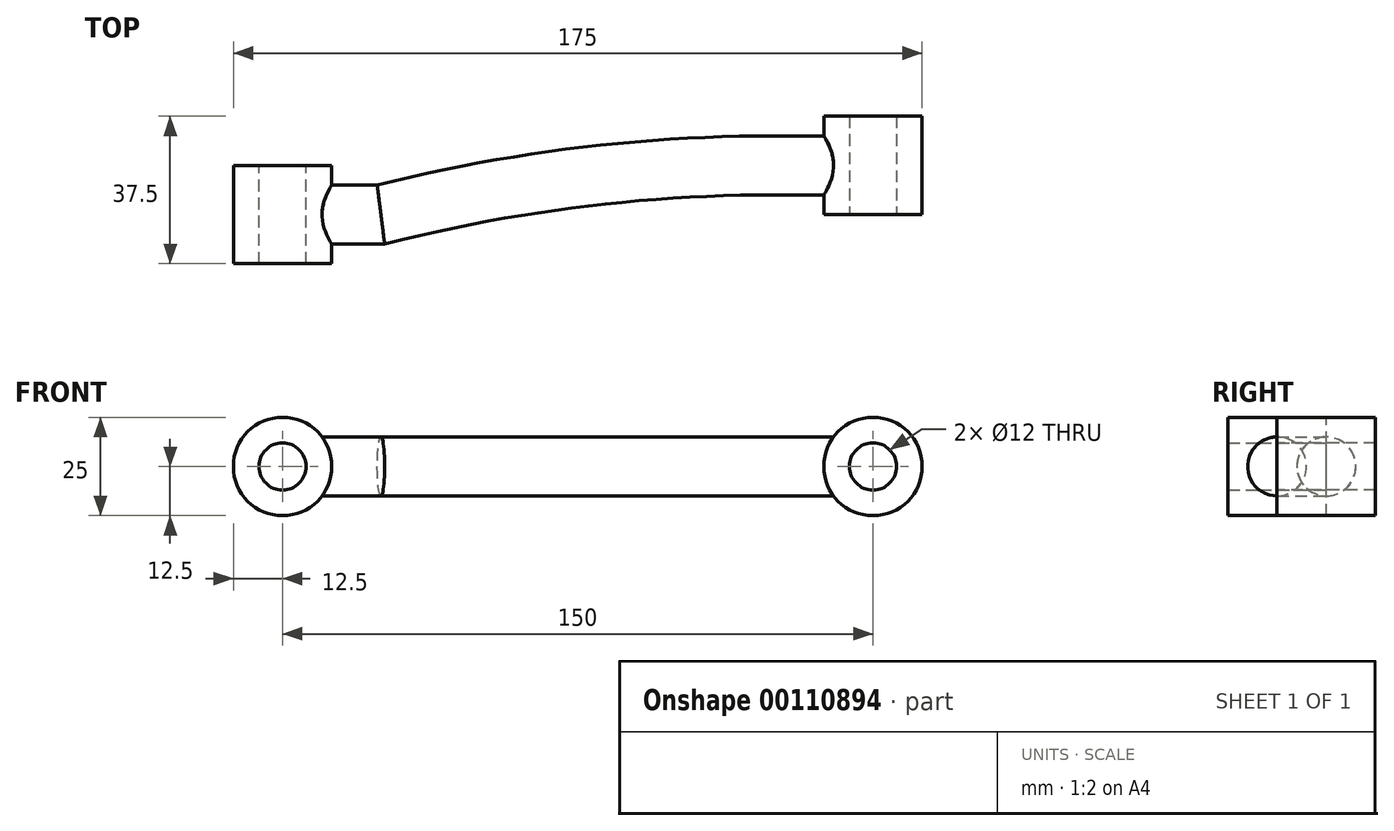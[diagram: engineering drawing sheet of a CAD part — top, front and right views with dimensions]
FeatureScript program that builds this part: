
annotation { "Feature Type Name" : "Feature", "Feature Type Description" : "" }
export const myFeature = defineFeature(function(context is Context, id is Id, definition is map)
    precondition{}
    {
        {
            var Q0;
            Q0=qCreatedBy(makeId("Front.planeOp"),FACE);
            var sketch = newSketch(context, id + "F0", { "sketchPlane" : qUnion([Q0])});
            skCircle(sketch, "E0", {"center": v(0, 0) * mm, "radius": 12.5 * mm});
            skCircle(sketch, "E1", {"center": v(0, 0) * mm, "radius": 6 * mm});
            skCircle(sketch, "E2", {"center": v(150, 0) * mm, "radius": 12.5 * mm});
            skCircle(sketch, "E3", {"center": v(150, 0) * mm, "radius": 6 * mm});
            skLineSegment(sketch, "E4", {"start": v(10, 7.5) * mm, "end": v(140, 7.5) * mm});
            skLineSegment(sketch, "E5", {"start": v(140, -7.5) * mm, "end": v(10, -7.5) * mm});
            skSolve(sketch);
        }
        {
            var Q0;
            Q0=qCreatedBy(makeId("Top.planeOp"),FACE);
            var sketch = newSketch(context, id + "F1", { "sketchPlane" : qUnion([Q0])});
            skLineSegment(sketch, "E6", {"start": v(0, 0) * mm, "end": v(25, 0) * mm});
            skArc(sketch, "E7", {"start": v(125, 12.5) * mm, "mid": v(74.61, 9.36) * mm, "end": v(25, 0) * mm});
            skLineSegment(sketch, "E8", {"start": v(125, 12.5) * mm, "end": v(150, 12.5) * mm});
            skSolve(sketch);
        }
        {
            var Q0;
            Q0=qCreatedBy(makeId("Right.planeOp"),FACE);
            var sketch = newSketch(context, id + "F2", { "sketchPlane" : qUnion([Q0])});
            skCircle(sketch, "E9", {"center": v(0, 0) * mm, "radius": 7.5 * mm});
            skSolve(sketch);
        }
        {
            var Q0;
            Q0=makeQuery(id+"F2.imprint","IMPRINT",FACE,{"disambiguationData":[TD([[makeQuery(id+"F2.imprint","IMPRINT",EDGE,{"derivedFrom":sQuery(id+"F2.wireOp",EDGE,"E9")}),1.0]])]});
            var Q1;
            Q1=sQuery(id+"F1.wireOp",EDGE,"E6");
            var Q2;
            Q2=sQuery(id+"F1.wireOp",EDGE,"E7");
            var Q3;
            Q3=sQuery(id+"F1.wireOp",EDGE,"E8");
            sweep(context, id + "F3", {"profiles" : qUnion([Q0]), "path" : qUnion([Q1, Q2, Q3])});
        }
        {
            var Q0;
            Q0=makeQuery(id+"F0.imprint","IMPRINT",FACE,{"disambiguationData":[TD([[makeQuery(id+"F0.imprint","IMPRINT",EDGE,{"derivedFrom":sQuery(id+"F0.wireOp",EDGE,"E1")}),-1.0]])]});
            extrude(context, id + "F4", {"entities" : qUnion([Q0]), "operationType" : NewBodyOperationType.ADD, "endBound" : BoundingType.SYMMETRIC, "depth" : 25 * mm});
        }
        {
            var Q0;
            Q0=makeQuery(id+"F0.imprint","IMPRINT",FACE,{"disambiguationData":[TD([[makeQuery(id+"F0.imprint","IMPRINT",EDGE,{"derivedFrom":sQuery(id+"F0.wireOp",EDGE,"E1")}),1.0]])]});
            extrude(context, id + "F5", {"entities" : qUnion([Q0]), "operationType" : NewBodyOperationType.REMOVE, "endBound" : BoundingType.THROUGH_ALL, "oppositeDirection" : true, "depth" : 25 * mm});
        }
        {
            var Q0;
            Q0=makeQuery(id+"F0.imprint","IMPRINT",FACE,{"disambiguationData":[TD([[makeQuery(id+"F0.imprint","IMPRINT",EDGE,{"derivedFrom":sQuery(id+"F0.wireOp",EDGE,"E1")}),1.0]])]});
            extrude(context, id + "F6", {"entities" : qUnion([Q0]), "operationType" : NewBodyOperationType.REMOVE, "endBound" : BoundingType.THROUGH_ALL, "depth" : 25 * mm});
        }
        {
            var Q0;
            Q0=makeQuery(id+"F0.imprint","IMPRINT",FACE,{"disambiguationData":[TD([[makeQuery(id+"F0.imprint","IMPRINT",EDGE,{"derivedFrom":sQuery(id+"F0.wireOp",EDGE,"E3")}),1.0]])]});
            extrude(context, id + "F7", {"entities" : qUnion([Q0]), "operationType" : NewBodyOperationType.REMOVE, "endBound" : BoundingType.THROUGH_ALL, "oppositeDirection" : true, "depth" : 25 * mm});
        }
        {
            var Q0;
            Q0=makeQuery(id+"F0.imprint","IMPRINT",FACE,{"disambiguationData":[TD([[makeQuery(id+"F0.imprint","IMPRINT",EDGE,{"derivedFrom":sQuery(id+"F0.wireOp",EDGE,"E3")}),-1.0]])]});
            extrude(context, id + "F8", {"entities" : qUnion([Q0]), "operationType" : NewBodyOperationType.ADD, "oppositeDirection" : true, "depth" : 25 * mm});
        }
    });
